# Revit family: PRD_AR_MxrTps_DoubleClampingBridge_ACXM1004 2
name_source: partatom
category: Specialty Equipment
units: mm (PartAtom-declared; Revit-internal decimal feet)

## family parameters
Always vertical = Yes
Cut with Voids When Loaded = No
Enable Cutting in Views = No
Maintain Annotation Orientation = No
OmniClass Number = 23.45.55.11
OmniClass Title = Sanitary Components
Part Type = Normal
Room Calculation Point = No
Round Connector Dimension = Use Diameter
Shared = No
Work Plane-Based = No

## types (1)
- ACXM1004
    AssetType = Fixed
    BIMObjectName = PRD_AR_MixerTaps_DoubleClampingBridge_ACXM1004
    BodyMaterial = PRD_AR_ChromatedBrass_HighPolished
    Category = PR_40_20_87_55, Mixer taps
    Default Elevation = 0 mm  [stored 0 ft]
    Description = Double clamping bridge for washbasin mixers with water connections positioned arranged side by side, for installation on distribution lines positioned next to one another, diameter 45 mm.
    Export Type to IFC As = IfcDiscreteAccessoryType
    Features = For washbasin mixers with water connections positioned arranged side by side.
    Finish = polished
    IfcExportAs = IfcDiscreteAccessory
    IfcExportType = BRACKET
    IsExternal = No
    IsInsulated = No
    Manufacturer = KWC Group Management AG
    ManufacturerName = KWC Group Management AG
    ManufacturerURL = www.kwc-professional.com
    Material = chrome-plated brass
    Model = ACXM1004
    ModelNumber = 2030059971
    ModelReference = ACXM1004
    NBSDescription = Taps and water supply fittings for wash basins and troughs
    NBSReference = 45-35-70/345
    Name = Double clamping bridge ACXM1004
    NominalDepth = 130 mm  [stored 0.426509 ft]
    NominalHeight = 72 mm  [stored 0.23622 ft]
    NominalWidth = 50 mm  [stored 0.164042 ft]
    ProductInformation = http://pim.kwc.com
    Quantity = 1
    QuantityUOM = piece
    Status = New
    Type IFC Predefined Type = BRACKET
    URL = www.kwc-professional.com
    Uniclass2015Code = Pr_40_20_87_55
    Uniclass2015Title = Mixer taps
    Uniclass2015Version = Products v1.38
    Version = 1

note: [stored X ft] marks values corroborated as IEEE doubles in the binary element streams (Revit-internal decimal feet)

## geometry (parser evidence)
native form markers: Sweep x5
no freeform markers — native parametric forms only
